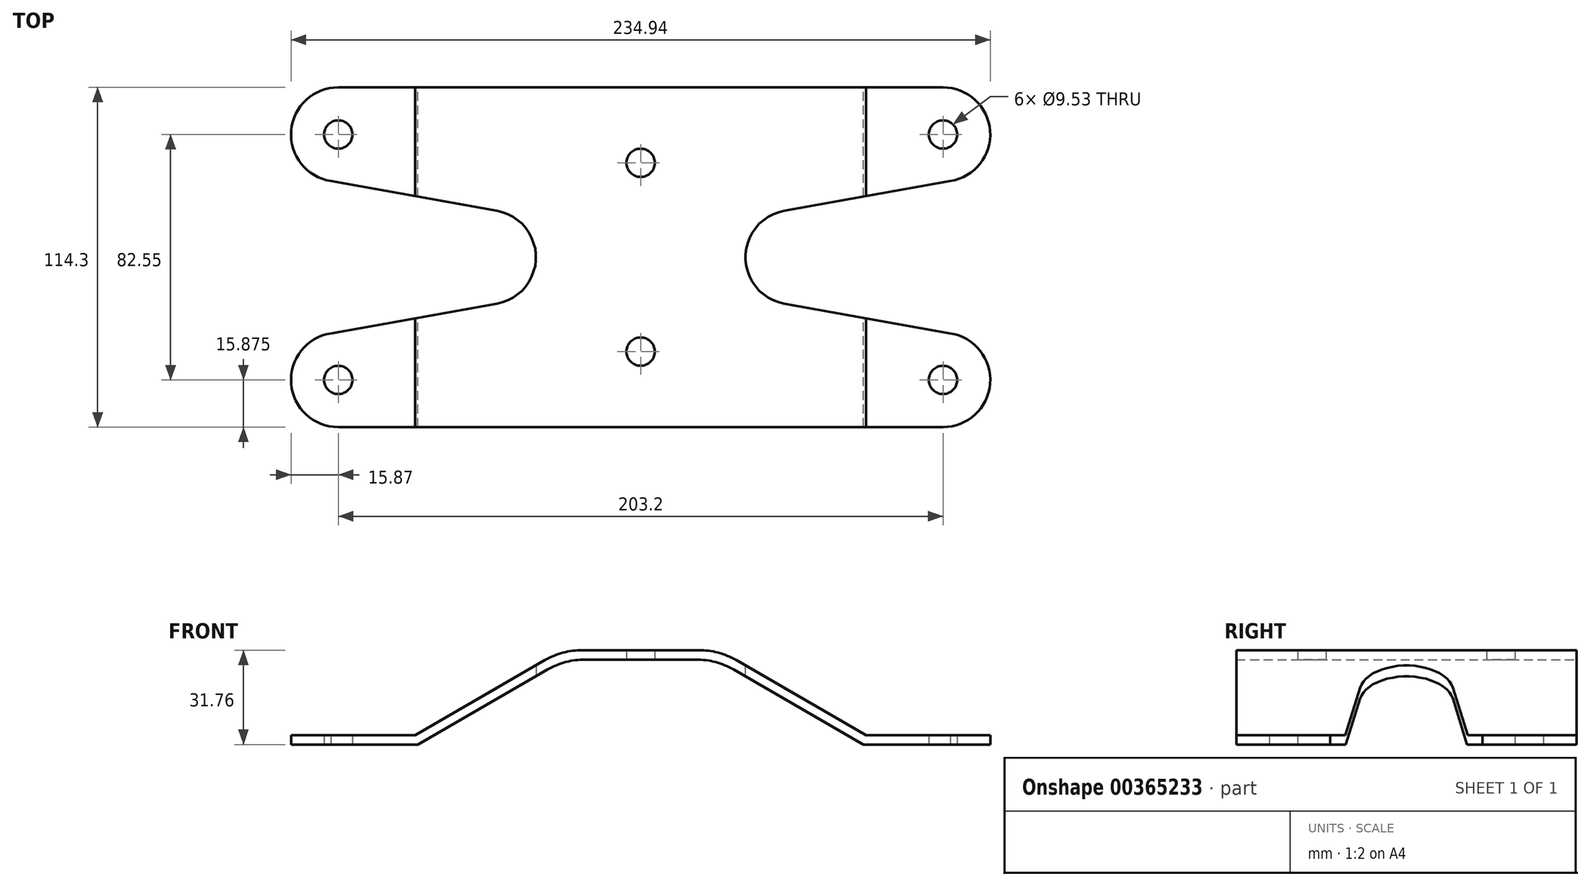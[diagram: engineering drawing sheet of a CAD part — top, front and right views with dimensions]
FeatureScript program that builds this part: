
annotation { "Feature Type Name" : "Feature", "Feature Type Description" : "" }
export const myFeature = defineFeature(function(context is Context, id is Id, definition is map)
    precondition{}
    {
        {
            var Q0;
            Q0=qCreatedBy(makeId("Front.planeOp"),FACE);
            var sketch = newSketch(context, id + "F0", { "sketchPlane" : qUnion([Q0])});
            skLineSegment(sketch, "E0", {"start": v(0, 0) * mm, "end": v(0, 57.11) * mm, "construction": true});
            skLineSegment(sketch, "E1", {"start": v(0, 0) * mm, "end": v(-25.4, 0) * mm});
            skLineSegment(sketch, "E2", {"start": v(-25.4, 0) * mm, "end": v(-74.9, -28.58) * mm});
            skLineSegment(sketch, "E3", {"start": v(-74.9, -28.58) * mm, "end": v(-127, -28.58) * mm});
            skLineSegment(sketch, "E4", {"start": v(-127, -28.58) * mm, "end": v(-127, -25.4) * mm});
            skLineSegment(sketch, "E5.0", {"start": v(-75.74, -25.4) * mm, "end": v(-127, -25.4) * mm});
            skLineSegment(sketch, "E5.1", {"start": v(-26.25, 3.18) * mm, "end": v(-75.74, -25.4) * mm});
            skLineSegment(sketch, "E5.2", {"start": v(0, 3.18) * mm, "end": v(-26.25, 3.17) * mm});
            skLineSegment(sketch, "E6.MirrorCS", {"start": v(127, -28.58) * mm, "end": v(127, -25.4) * mm});
            skLineSegment(sketch, "E7.MirrorCS", {"start": v(74.9, -28.58) * mm, "end": v(127, -28.58) * mm});
            skLineSegment(sketch, "E8.MirrorCS", {"start": v(75.74, -25.4) * mm, "end": v(127, -25.4) * mm});
            skLineSegment(sketch, "E9.MirrorCS", {"start": v(26.25, 3.18) * mm, "end": v(75.74, -25.4) * mm});
            skLineSegment(sketch, "E10.MirrorCS", {"start": v(0, 0) * mm, "end": v(25.4, 0) * mm});
            skLineSegment(sketch, "E11.MirrorCS", {"start": v(25.4, 0) * mm, "end": v(74.9, -28.58) * mm});
            skLineSegment(sketch, "E12.MirrorCS", {"start": v(0, 3.18) * mm, "end": v(26.25, 3.17) * mm});
            skSolve(sketch);
        }
        {
            var Q0;
            Q0 = qSketchRegion(id + "F0", true);
            extrude(context, id + "F1", {"entities" : qUnion([Q0]), "depth" : 63.5 * mm, "hasSecondDirection" : true, "secondDirectionOppositeDirection" : true, "secondDirectionDepth" : 74.68 * mm});
        }
        {
            var Q0;
            Q0=qCreatedBy(makeId("Top.planeOp"),FACE);
            var sketch = newSketch(context, id + "F2", { "sketchPlane" : qUnion([Q0])});
            skLineSegment(sketch, "E13", {"start": v(0, 0) * mm, "end": v(187.03, 0) * mm, "construction": true});
            skLineSegment(sketch, "E14", {"start": v(-167.64, -57.15) * mm, "end": v(179.82, -57.15) * mm});
            skArc(sketch, "E15", {"start": v(101.6, -57.15) * mm, "mid": v(117.43, -42.52) * mm, "end": v(104.07, -25.6) * mm});
            skLineSegment(sketch, "E16", {"start": v(0, 0) * mm, "end": v(0, -103.82) * mm, "construction": true});
            skArc(sketch, "E17", {"start": v(48.24, 15.63) * mm, "mid": v(35.15, 0) * mm, "end": v(48.24, -15.63) * mm});
            skLineSegment(sketch, "E18", {"start": v(104.07, -25.6) * mm, "end": v(48.24, -15.63) * mm});
            skLineSegment(sketch, "E19", {"start": v(0, -57.15) * mm, "end": v(101.6, -57.15) * mm});
            skLineSegment(sketch, "E20.MirrorCS", {"start": v(0, 57.15) * mm, "end": v(101.6, 57.15) * mm});
            skArc(sketch, "E21.MirrorC", {"start": v(101.6, 57.15) * mm, "mid": v(117.43, 42.52) * mm, "end": v(104.07, 25.6) * mm});
            skLineSegment(sketch, "E22.MirrorCS", {"start": v(104.07, 25.6) * mm, "end": v(48.24, 15.63) * mm});
            skLineSegment(sketch, "E23.MirrorCS", {"start": v(0, 57.15) * mm, "end": v(-101.6, 57.15) * mm});
            skArc(sketch, "E24.MirrorC", {"start": v(-101.6, 57.15) * mm, "mid": v(-117.43, 42.52) * mm, "end": v(-104.07, 25.6) * mm});
            skLineSegment(sketch, "E25.MirrorCS", {"start": v(-104.07, 25.6) * mm, "end": v(-48.24, 15.63) * mm});
            skArc(sketch, "E26.MirrorC", {"start": v(-48.24, 15.63) * mm, "mid": v(-35.15, 0) * mm, "end": v(-48.24, -15.63) * mm});
            skLineSegment(sketch, "E27.MirrorCS", {"start": v(-104.07, -25.6) * mm, "end": v(-48.24, -15.63) * mm});
            skArc(sketch, "E28.MirrorC", {"start": v(-101.6, -57.15) * mm, "mid": v(-117.43, -42.52) * mm, "end": v(-104.07, -25.6) * mm});
            skLineSegment(sketch, "E29.MirrorCS", {"start": v(0, -57.15) * mm, "end": v(-101.6, -57.15) * mm});
            skCircle(sketch, "E30", {"center": v(-101.6, -41.28) * mm, "radius": 4.76 * mm});
            skCircle(sketch, "E31", {"center": v(-101.6, 41.28) * mm, "radius": 4.76 * mm});
            skCircle(sketch, "E32", {"center": v(101.6, 41.28) * mm, "radius": 4.76 * mm});
            skCircle(sketch, "E33", {"center": v(101.6, -41.28) * mm, "radius": 4.76 * mm});
            skCircle(sketch, "E34", {"center": v(0, 31.75) * mm, "radius": 4.76 * mm});
            skCircle(sketch, "E35.MirrorC", {"center": v(0, -31.75) * mm, "radius": 4.76 * mm});
            skSolve(sketch);
        }
        {
            var Q0;
            Q0 = qSketchRegion(id + "F2", true);
            extrude(context, id + "F3", {"entities" : qUnion([Q0]), "operationType" : NewBodyOperationType.INTERSECT, "depth" : 104.65 * mm, "hasSecondDirection" : true, "secondDirectionOppositeDirection" : true, "secondDirectionDepth" : 145.54 * mm});
        }
        {
            var Q0;
            {var subQ0=sQuery(id+"F0.wireOp",EDGE,"E5.0");var subQ1=sQuery(id+"F0.wireOp",EDGE,"E5.1");Q0=makeQuery(id+"F3.boolean.opBoolean","SPLIT",EDGE,{"disambiguationData":[TD([makeQuery(id+"F3.boolean.toolComplement.opBoolean","COPY",FACE,{"derivedFrom":makeQuery(id+"F3.opExtrude","SWEPT_FACE",FACE,{"disambiguationData":[OSD([sQuery(id+"F2.wireOp",EDGE,"E25.MirrorCS")])]})})])],"derivedFrom":makeQuery(id+"F1.opExtrude","SWEPT_EDGE",EDGE,{"disambiguationData":[OSD([subQ0,subQ1])]})});}
            var Q1;
            {var subQ0=sQuery(id+"F0.wireOp",EDGE,"E5.0");var subQ1=sQuery(id+"F0.wireOp",EDGE,"E5.1");Q1=makeQuery(id+"F3.boolean.opBoolean","SPLIT",EDGE,{"disambiguationData":[TD([makeQuery(id+"F3.boolean.toolComplement.opBoolean","COPY",FACE,{"derivedFrom":makeQuery(id+"F3.opExtrude","SWEPT_FACE",FACE,{"disambiguationData":[OSD([sQuery(id+"F2.wireOp",EDGE,"E27.MirrorCS")])]})})])],"derivedFrom":makeQuery(id+"F1.opExtrude","SWEPT_EDGE",EDGE,{"disambiguationData":[OSD([subQ0,subQ1])]})});}
            var Q2;
            Q2=makeQuery(id+"F1.opExtrude","SWEPT_EDGE",EDGE,{"disambiguationData":[OSD([sQuery(id+"F0.wireOp",EDGE,"E5.1"),sQuery(id+"F0.wireOp",EDGE,"E5.2")])]});
            var Q3;
            Q3=makeQuery(id+"F1.opExtrude","SWEPT_EDGE",EDGE,{"disambiguationData":[OSD([sQuery(id+"F0.wireOp",EDGE,"E9.MirrorCS"),sQuery(id+"F0.wireOp",EDGE,"E12.MirrorCS")])]});
            var Q4;
            {var subQ0=sQuery(id+"F0.wireOp",EDGE,"E8.MirrorCS");var subQ1=sQuery(id+"F0.wireOp",EDGE,"E9.MirrorCS");Q4=makeQuery(id+"F3.boolean.opBoolean","SPLIT",EDGE,{"disambiguationData":[TD([makeQuery(id+"F3.boolean.toolComplement.opBoolean","COPY",FACE,{"derivedFrom":makeQuery(id+"F3.opExtrude","SWEPT_FACE",FACE,{"disambiguationData":[OSD([sQuery(id+"F2.wireOp",EDGE,"E22.MirrorCS")])]})})])],"derivedFrom":makeQuery(id+"F1.opExtrude","SWEPT_EDGE",EDGE,{"disambiguationData":[OSD([subQ0,subQ1])]})});}
            var Q5;
            {var subQ0=sQuery(id+"F0.wireOp",EDGE,"E8.MirrorCS");var subQ1=sQuery(id+"F0.wireOp",EDGE,"E9.MirrorCS");Q5=makeQuery(id+"F3.boolean.opBoolean","SPLIT",EDGE,{"disambiguationData":[TD([makeQuery(id+"F3.boolean.toolComplement.opBoolean","COPY",FACE,{"derivedFrom":makeQuery(id+"F3.opExtrude","SWEPT_FACE",FACE,{"disambiguationData":[OSD([sQuery(id+"F2.wireOp",EDGE,"E18")])]})})])],"derivedFrom":makeQuery(id+"F1.opExtrude","SWEPT_EDGE",EDGE,{"disambiguationData":[OSD([subQ0,subQ1])]})});}
            var Q6;
            Q6=makeQuery(id+"F1.opExtrude","SWEPT_EDGE",EDGE,{"disambiguationData":[OSD([sQuery(id+"F0.wireOp",EDGE,"E1"),sQuery(id+"F0.wireOp",EDGE,"E2")])]});
            var Q7;
            Q7=makeQuery(id+"F1.opExtrude","SWEPT_EDGE",EDGE,{"disambiguationData":[OSD([sQuery(id+"F0.wireOp",EDGE,"E10.MirrorCS"),sQuery(id+"F0.wireOp",EDGE,"E11.MirrorCS")])]});
            fillet(context, id + "F4", {"entities" : qUnion([Q0, Q1, Q2, Q3, Q4, Q5, Q6, Q7]), "radius" : 25.4 * mm, "tangentPropagation" : true, "allowEdgeOverflow" : false});
        }
    });
